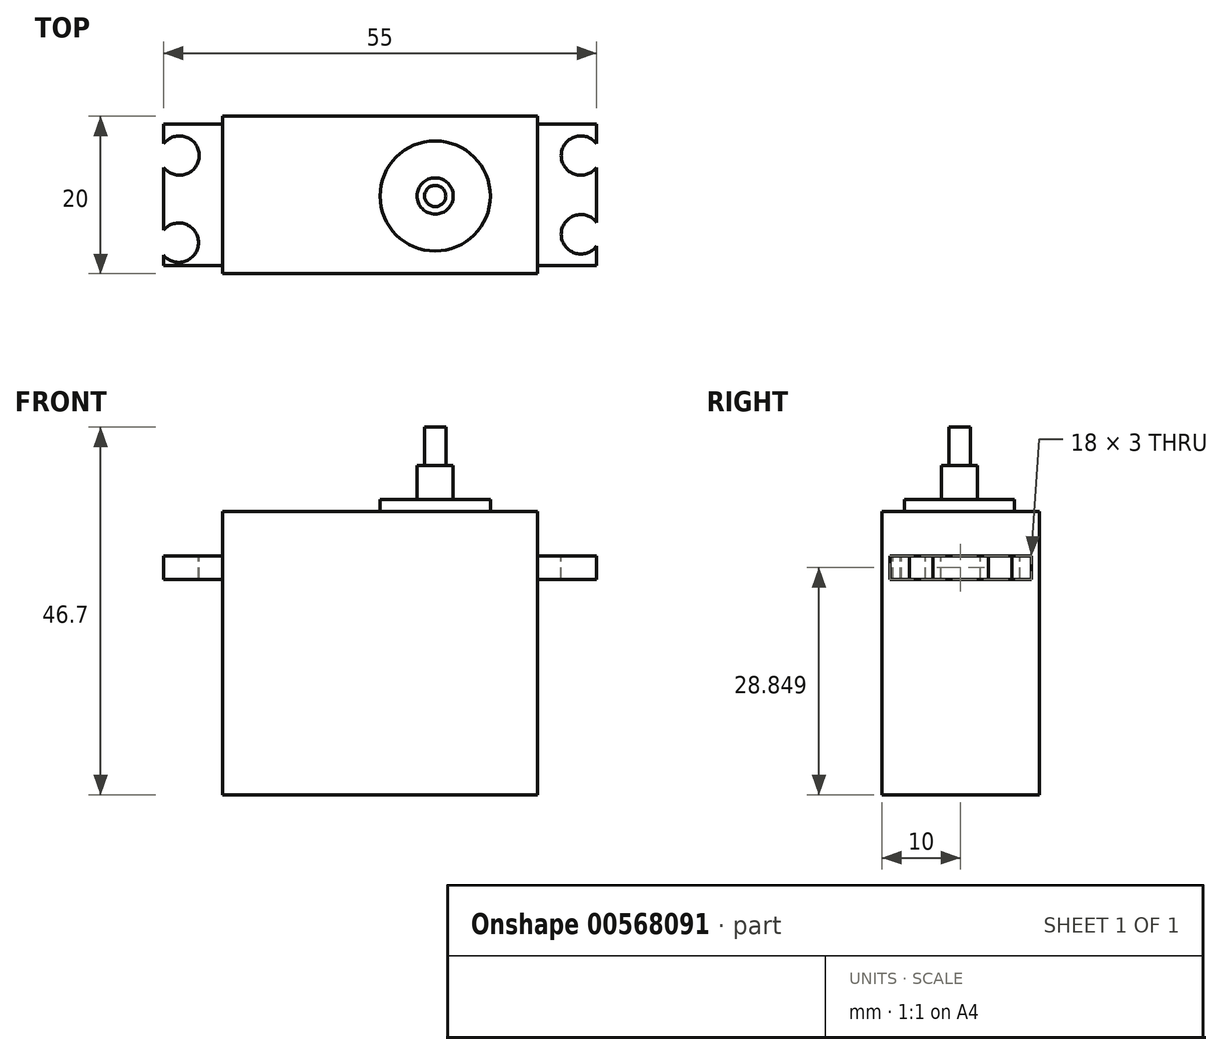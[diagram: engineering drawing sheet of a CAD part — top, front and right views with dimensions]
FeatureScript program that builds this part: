
annotation { "Feature Type Name" : "Feature", "Feature Type Description" : "" }
export const myFeature = defineFeature(function(context is Context, id is Id, definition is map)
    precondition{}
    {
        {
            var Q0;
            Q0=qCreatedBy(makeId("Top.planeOp"),FACE);
            var sketch = newSketch(context, id + "F0", { "sketchPlane" : qUnion([Q0])});
            skLineSegment(sketch, "E0.bottom", {"start": v(-19.27, 4.13) * mm, "end": v(20.73, 4.13) * mm});
            skLineSegment(sketch, "E0.top", {"start": v(-19.27, -15.87) * mm, "end": v(20.73, -15.87) * mm});
            skLineSegment(sketch, "E0.left", {"start": v(-19.27, 4.13) * mm, "end": v(-19.27, -15.87) * mm});
            skLineSegment(sketch, "E0.right", {"start": v(20.73, 4.13) * mm, "end": v(20.73, -15.87) * mm});
            skSolve(sketch);
        }
        {
            var Q0;
            Q0=makeQuery(id+"F0.imprint","IMPRINT",FACE,{"disambiguationData":[TD([[makeQuery(id+"F0.imprint","IMPRINT",EDGE,{"derivedFrom":sQuery(id+"F0.wireOp",EDGE,"E0.bottom")}),-1.0]])]});
            extrude(context, id + "F1", {"entities" : qUnion([Q0]), "depth" : 36 * mm, "offsetDistance" : 25 * mm});
        }
        {
            var Q0;
            Q0=makeQuery(id+"F1.opExtrude","SWEPT_FACE",FACE,{"disambiguationData":[OSD([sQuery(id+"F0.wireOp",EDGE,"E0.right")])]});
            var sketch = newSketch(context, id + "F2", { "sketchPlane" : qUnion([Q0])});
            skLineSegment(sketch, "E1.bottom", {"start": v(-14.87, 30.35) * mm, "end": v(3.13, 30.35) * mm});
            skLineSegment(sketch, "E1.top", {"start": v(-14.87, 27.35) * mm, "end": v(3.13, 27.35) * mm});
            skLineSegment(sketch, "E1.left", {"start": v(-14.87, 30.35) * mm, "end": v(-14.87, 27.35) * mm});
            skLineSegment(sketch, "E1.right", {"start": v(3.13, 30.35) * mm, "end": v(3.13, 27.35) * mm});
            skSolve(sketch);
        }
        {
            var Q0;
            Q0=makeQuery(id+"F2.imprint","IMPRINT",FACE,{"disambiguationData":[TD([[makeQuery(id+"F2.imprint","IMPRINT",EDGE,{"derivedFrom":sQuery(id+"F2.wireOp",EDGE,"E1.bottom")}),-1.0]])]});
            extrude(context, id + "F3", {"entities" : qUnion([Q0]), "operationType" : NewBodyOperationType.ADD, "depth" : 7.5 * mm, "offsetDistance" : 25 * mm});
        }
        {
            var Q0;
            Q0=makeQuery(id+"F1.opExtrude","SWEPT_FACE",FACE,{"disambiguationData":[OSD([sQuery(id+"F0.wireOp",EDGE,"E0.left")])]});
            var sketch = newSketch(context, id + "F4", { "sketchPlane" : qUnion([Q0])});
            skLineSegment(sketch, "E2.bottom", {"start": v(-3.13, 27.36) * mm, "end": v(14.87, 27.36) * mm});
            skLineSegment(sketch, "E2.top", {"start": v(-3.13, 30.35) * mm, "end": v(14.87, 30.35) * mm});
            skLineSegment(sketch, "E2.left", {"start": v(-3.13, 27.36) * mm, "end": v(-3.13, 30.35) * mm});
            skLineSegment(sketch, "E2.right", {"start": v(14.87, 27.36) * mm, "end": v(14.87, 30.35) * mm});
            skSolve(sketch);
        }
        {
            var Q0;
            Q0 = qSketchRegion(id + "F4", true);
            extrude(context, id + "F5", {"entities" : qUnion([Q0]), "operationType" : NewBodyOperationType.ADD, "depth" : 7.5 * mm, "offsetDistance" : 25 * mm});
        }
        {
            var Q0;
            Q0=makeQuery(id+"F5.opExtrude","SWEPT_FACE",FACE,{"disambiguationData":[OSD([sQuery(id+"F4.wireOp",EDGE,"E2.top")])]});
            var sketch = newSketch(context, id + "F6", { "sketchPlane" : qUnion([Q0])});
            skCircle(sketch, "E3", {"center": v(-24.84, -11.94) * mm, "radius": 1.54 * mm});
            skCircle(sketch, "E4", {"center": v(-24.64, -2.46) * mm, "radius": 1.68 * mm});
            skSolve(sketch);
        }
        {
            var Q0;
            Q0=makeQuery(id+"F5.opExtrude","SWEPT_FACE",FACE,{"disambiguationData":[OSD([sQuery(id+"F4.wireOp",EDGE,"E2.top")])]});
            var sketch = newSketch(context, id + "F7", { "sketchPlane" : qUnion([Q0])});
            skCircle(sketch, "E5", {"center": v(-24.77, -0.87) * mm, "radius": 2.5 * mm});
            skCircle(sketch, "E6", {"center": v(26.23, -0.87) * mm, "radius": 2.5 * mm});
            skCircle(sketch, "E7", {"center": v(26.23, -10.87) * mm, "radius": 2.5 * mm});
            skCircle(sketch, "E8", {"center": v(-24.77, -10.87) * mm, "radius": 2.5 * mm});
            skSolve(sketch);
        }
        {
            var Q0;
            Q0=sQuery(id+"F7.wireOp",VERTEX,"E5.center");
            var Q1;
            Q1=sQuery(id+"F6.wireOp",VERTEX,"E3.center");
            var Q2;
            Q2=sQuery(id+"F7.wireOp",VERTEX,"E7.center");
            var Q3;
            Q3=sQuery(id+"F7.wireOp",VERTEX,"E6.center");
            var Q4;
            Q4=makeQuery(id+"F1.opExtrude","SWEPT_BODY",BODY,{"disambiguationData":[OSD([sQuery(id+"F0.wireOp",EDGE,"E0.bottom"),sQuery(id+"F0.wireOp",EDGE,"E0.top"),sQuery(id+"F0.wireOp",EDGE,"E0.left"),sQuery(id+"F0.wireOp",EDGE,"E0.right")])]});
            hole(context, id + "F8", {"style" : HoleStyle.SIMPLE, "endStyle" : HoleEndStyle.THROUGH, "holeDiameter" : 5 * mm, "isTappedThrough" : true, "tappedDepth" : 12 * mm, "tapClearance" : 3, "locations" : qUnion([Q0, Q1, Q2, Q3]), "scope" : qUnion([Q4])});
        }
        {
            var Q0;
            Q0=makeQuery(id+"F1.opExtrude","CAP_FACE",FACE,{"disambiguationData":[OSD([sQuery(id+"F0.wireOp",EDGE,"E0.bottom"),sQuery(id+"F0.wireOp",EDGE,"E0.top"),sQuery(id+"F0.wireOp",EDGE,"E0.left"),sQuery(id+"F0.wireOp",EDGE,"E0.right")])],"isStart":false});
            var sketch = newSketch(context, id + "F9", { "sketchPlane" : qUnion([Q0])});
            skCircle(sketch, "E9", {"center": v(7.72, -6) * mm, "radius": 7 * mm});
            skSolve(sketch);
        }
        {
            var Q0;
            Q0 = qSketchRegion(id + "F9", true);
            extrude(context, id + "F10", {"entities" : qUnion([Q0]), "operationType" : NewBodyOperationType.ADD, "depth" : 1.5 * mm, "offsetDistance" : 25 * mm});
        }
        {
            var Q0;
            Q0=makeQuery(id+"F10.opExtrude","CAP_FACE",FACE,{"disambiguationData":[OSD([sQuery(id+"F9.wireOp",EDGE,"E9")])],"isStart":false});
            var sketch = newSketch(context, id + "F11", { "sketchPlane" : qUnion([Q0])});
            skCircle(sketch, "E10", {"center": v(7.72, -6) * mm, "radius": 2.3 * mm});
            skSolve(sketch);
        }
        {
            var Q0;
            Q0 = qSketchRegion(id + "F11", true);
            extrude(context, id + "F12", {"entities" : qUnion([Q0]), "operationType" : NewBodyOperationType.ADD, "depth" : 4.3 * mm, "offsetDistance" : 25 * mm});
        }
        {
            var Q0;
            Q0=makeQuery(id+"F12.opExtrude","CAP_FACE",FACE,{"disambiguationData":[OSD([sQuery(id+"F11.wireOp",EDGE,"E10")])],"isStart":false});
            var sketch = newSketch(context, id + "F13", { "sketchPlane" : qUnion([Q0])});
            skCircle(sketch, "E11", {"center": v(7.72, -6) * mm, "radius": 1.35 * mm});
            skSolve(sketch);
        }
        {
            var Q0;
            Q0=makeQuery(id+"F13.imprint","IMPRINT",FACE,{"disambiguationData":[TD([[makeQuery(id+"F13.imprint","IMPRINT",EDGE,{"derivedFrom":sQuery(id+"F13.wireOp",EDGE,"E11")}),1.0]])]});
            extrude(context, id + "F14", {"entities" : qUnion([Q0]), "operationType" : NewBodyOperationType.ADD, "depth" : 4.9 * mm, "offsetDistance" : 25 * mm});
        }
    });
